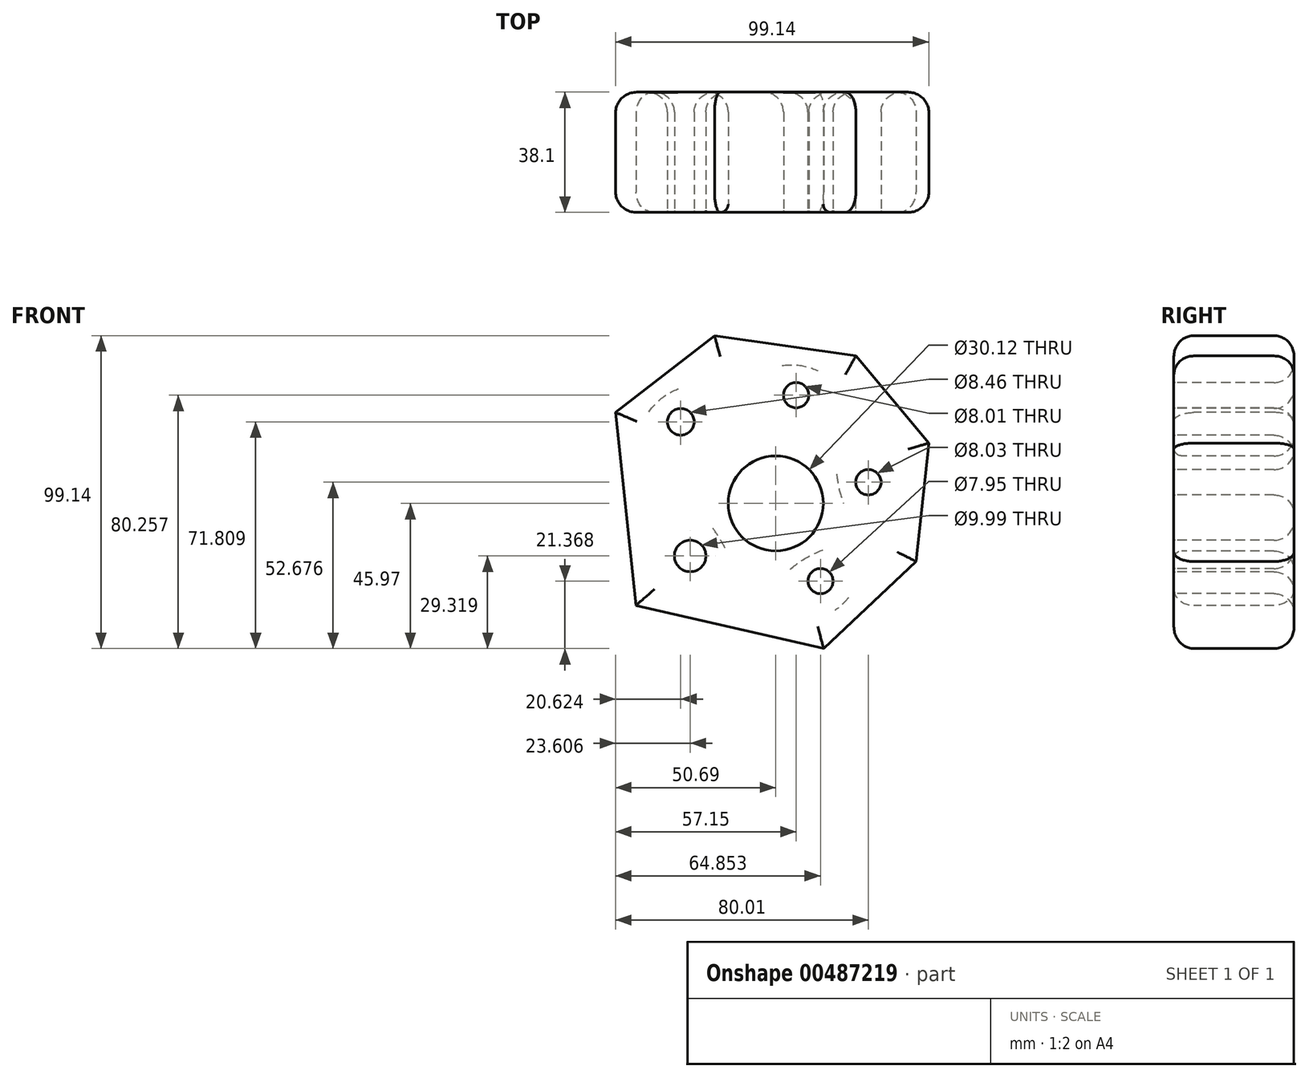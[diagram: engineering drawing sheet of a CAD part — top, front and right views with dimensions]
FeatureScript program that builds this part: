
annotation { "Feature Type Name" : "Feature", "Feature Type Description" : "" }
export const myFeature = defineFeature(function(context is Context, id is Id, definition is map)
    precondition{}
    {
        {
            var Q0;
            Q0=qCreatedBy(makeId("Front.planeOp"),FACE);
            var sketch = newSketch(context, id + "F0", { "sketchPlane" : qUnion([Q0])});
            skLineSegment(sketch, "E0", {"start": v(-44.23, -32.3) * mm, "end": v(15.16, -45.97) * mm});
            skLineSegment(sketch, "E1", {"start": v(15.16, -45.97) * mm, "end": v(44.48, -18.39) * mm});
            skLineSegment(sketch, "E2", {"start": v(44.48, -18.39) * mm, "end": v(48.45, 19.13) * mm});
            skLineSegment(sketch, "E3", {"start": v(48.45, 19.13) * mm, "end": v(25.34, 46.71) * mm});
            skLineSegment(sketch, "E4", {"start": v(25.34, 46.71) * mm, "end": v(-19.38, 53.17) * mm});
            skLineSegment(sketch, "E5", {"start": v(-19.38, 53.17) * mm, "end": v(-50.69, 28.82) * mm});
            skLineSegment(sketch, "E6", {"start": v(-50.69, 28.82) * mm, "end": v(-44.23, -32.3) * mm});
            skCircle(sketch, "E7", {"center": v(0, 0) * mm, "radius": 15.06 * mm});
            skCircle(sketch, "E8", {"center": v(-30.07, 25.84) * mm, "radius": 4.23 * mm});
            skCircle(sketch, "E9", {"center": v(6.46, 34.29) * mm, "radius": 4 * mm});
            skCircle(sketch, "E10", {"center": v(29.32, 6.7) * mm, "radius": 4.01 * mm});
            skCircle(sketch, "E11", {"center": v(14.16, -24.6) * mm, "radius": 3.98 * mm});
            skCircle(sketch, "E12", {"center": v(-27.08, -16.65) * mm, "radius": 5 * mm});
            skSolve(sketch);
        }
        {
            var Q0;
            Q0 = qSketchRegion(id + "F0", true);
            extrude(context, id + "F1", {"entities" : qUnion([Q0]), "oppositeDirection" : true, "depth" : 38.1 * mm});
        }
        {
            var Q0;
            Q0=makeQuery(id+"F1.opExtrude","CAP_EDGE",EDGE,{"disambiguationData":[OSD([sQuery(id+"F0.wireOp",EDGE,"E4")])],"isStart":true});
            var Q1;
            Q1=makeQuery(id+"F1.opExtrude","CAP_EDGE",EDGE,{"disambiguationData":[OSD([sQuery(id+"F0.wireOp",EDGE,"E3")])],"isStart":true});
            var Q2;
            Q2=makeQuery(id+"F1.opExtrude","CAP_EDGE",EDGE,{"disambiguationData":[OSD([sQuery(id+"F0.wireOp",EDGE,"E2")])],"isStart":true});
            var Q3;
            Q3=makeQuery(id+"F1.opExtrude","CAP_EDGE",EDGE,{"disambiguationData":[OSD([sQuery(id+"F0.wireOp",EDGE,"E1")])],"isStart":true});
            var Q4;
            Q4=makeQuery(id+"F1.opExtrude","CAP_EDGE",EDGE,{"disambiguationData":[OSD([sQuery(id+"F0.wireOp",EDGE,"E0")])],"isStart":true});
            var Q5;
            Q5=makeQuery(id+"F1.opExtrude","CAP_EDGE",EDGE,{"disambiguationData":[OSD([sQuery(id+"F0.wireOp",EDGE,"E6")])],"isStart":true});
            var Q6;
            Q6=makeQuery(id+"F1.opExtrude","CAP_EDGE",EDGE,{"disambiguationData":[OSD([sQuery(id+"F0.wireOp",EDGE,"E5")])],"isStart":true});
            var Q7;
            Q7=makeQuery(id+"F1.opExtrude","CAP_FACE",FACE,{"disambiguationData":[OSD([sQuery(id+"F0.wireOp",EDGE,"E0"),sQuery(id+"F0.wireOp",EDGE,"E1"),sQuery(id+"F0.wireOp",EDGE,"E2"),sQuery(id+"F0.wireOp",EDGE,"E3"),sQuery(id+"F0.wireOp",EDGE,"E4"),sQuery(id+"F0.wireOp",EDGE,"E5"),sQuery(id+"F0.wireOp",EDGE,"E6"),sQuery(id+"F0.wireOp",EDGE,"E7")])],"isStart":false});
            fillet(context, id + "F2", {"entities" : qUnion([Q0, Q1, Q2, Q3, Q4, Q5, Q6, Q7]), "radius" : 6.35 * mm, "tangentPropagation" : true, "allowEdgeOverflow" : false});
        }
        {
            var Q0;
            Q0=makeQuery(id+"F1.opExtrude","CAP_EDGE",EDGE,{"disambiguationData":[OSD([sQuery(id+"F0.wireOp",EDGE,"E7")])],"isStart":true});
            var Q1;
            {var subQ0=sQuery(id+"F0.wireOp",EDGE,"E7");Q1=makeQuery(id+"F2.opFillet","BLEND_EDGE",EDGE,{"blendedFrom":[makeQuery(id+"F1.opExtrude","CAP_EDGE",EDGE,{"disambiguationData":[OSD([subQ0])],"isStart":false}),makeQuery(id+"F1.opExtrude","SWEPT_FACE",FACE,{"disambiguationData":[OSD([subQ0])]})],"blendedInto":[makeQuery(id+"F1.opExtrude","SWEPT_FACE",FACE,{"disambiguationData":[OSD([subQ0])]})]});}
            fillet(context, id + "F3", {"entities" : qUnion([Q0, Q1]), "radius" : 2.54 * mm, "tangentPropagation" : true, "allowEdgeOverflow" : false});
        }
        {
            var Q0;
            Q0=makeQuery(id+"F1.opExtrude","CAP_EDGE",EDGE,{"disambiguationData":[OSD([sQuery(id+"F0.wireOp",EDGE,"E8")])],"isStart":true});
            var Q1;
            Q1=makeQuery(id+"F1.opExtrude","CAP_EDGE",EDGE,{"disambiguationData":[OSD([sQuery(id+"F0.wireOp",EDGE,"E9")])],"isStart":true});
            var Q2;
            Q2=makeQuery(id+"F1.opExtrude","CAP_EDGE",EDGE,{"disambiguationData":[OSD([sQuery(id+"F0.wireOp",EDGE,"E10")])],"isStart":true});
            var Q3;
            Q3=makeQuery(id+"F1.opExtrude","CAP_EDGE",EDGE,{"disambiguationData":[OSD([sQuery(id+"F0.wireOp",EDGE,"E11")])],"isStart":true});
            var Q4;
            Q4=makeQuery(id+"F1.opExtrude","CAP_EDGE",EDGE,{"disambiguationData":[OSD([sQuery(id+"F0.wireOp",EDGE,"E12")])],"isStart":true});
            fillet(context, id + "F4", {"entities" : qUnion([Q0, Q1, Q2, Q3, Q4]), "radius" : 0.5 * mm, "tangentPropagation" : true, "allowEdgeOverflow" : false});
        }
    });
